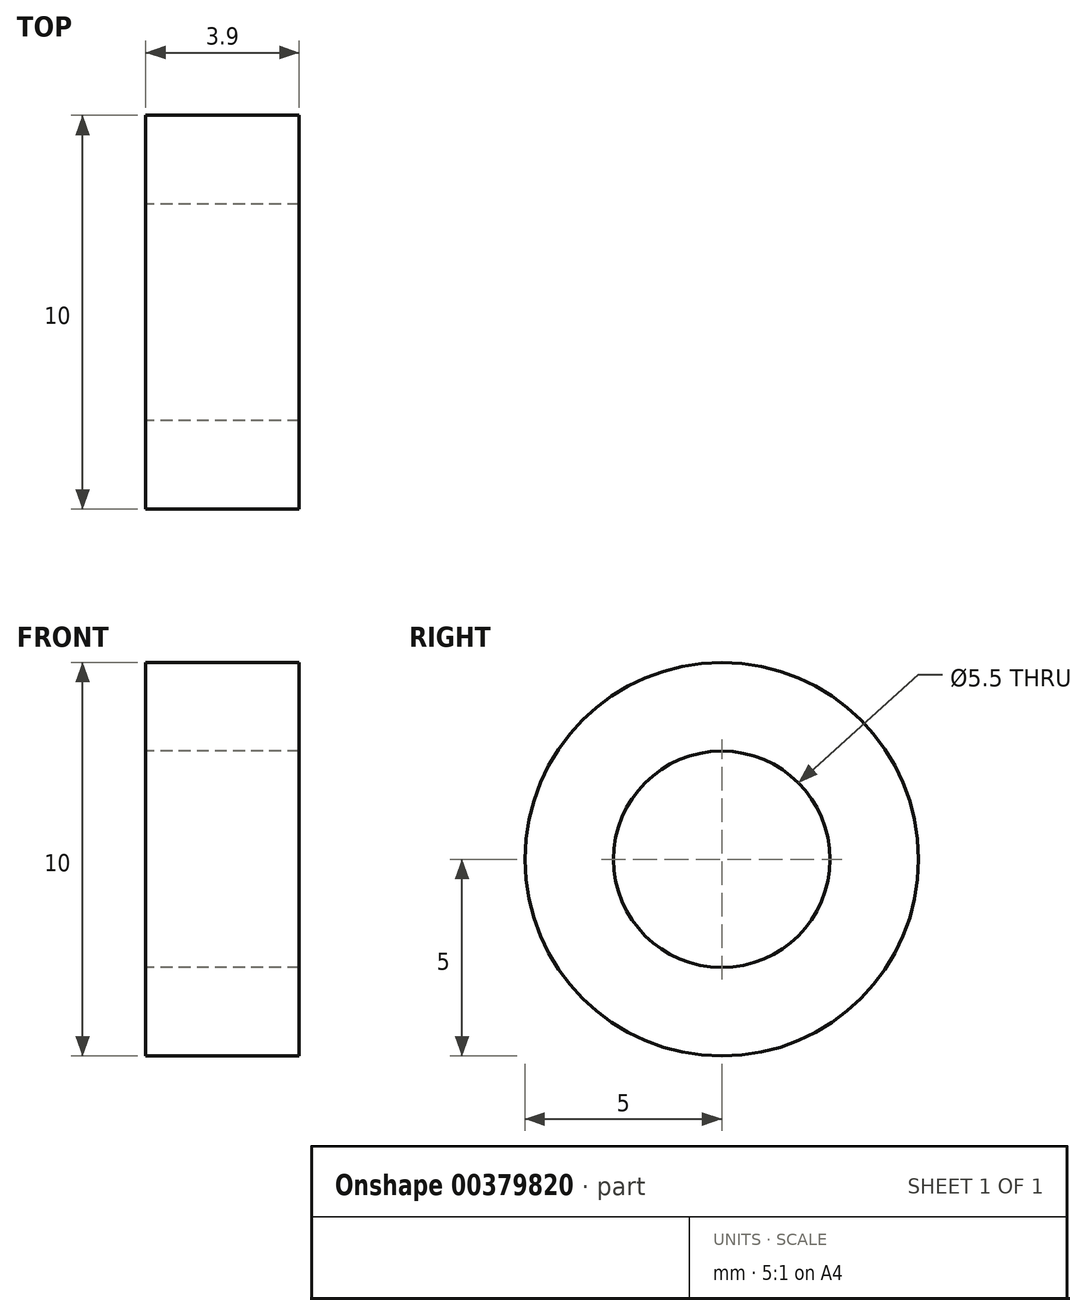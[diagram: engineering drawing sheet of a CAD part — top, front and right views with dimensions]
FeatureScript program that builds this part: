
annotation { "Feature Type Name" : "Feature", "Feature Type Description" : "" }
export const myFeature = defineFeature(function(context is Context, id is Id, definition is map)
    precondition{}
    {
        {
            var Q0;
            Q0=qCreatedBy(makeId("Right.planeOp"),FACE);
            var sketch = newSketch(context, id + "F0", { "sketchPlane" : qUnion([Q0])});
            skCircle(sketch, "E0", {"center": v(0, 0) * mm, "radius": 5 * mm});
            skCircle(sketch, "E1", {"center": v(0, 0) * mm, "radius": 2.75 * mm});
            skSolve(sketch);
        }
        {
            var Q0;
            Q0=qSketchRegion(id+"F0",true);
            extrude(context, id + "F1", {"entities" : qUnion([Q0]), "depth" : 3.9 * mm});
        }
    });
